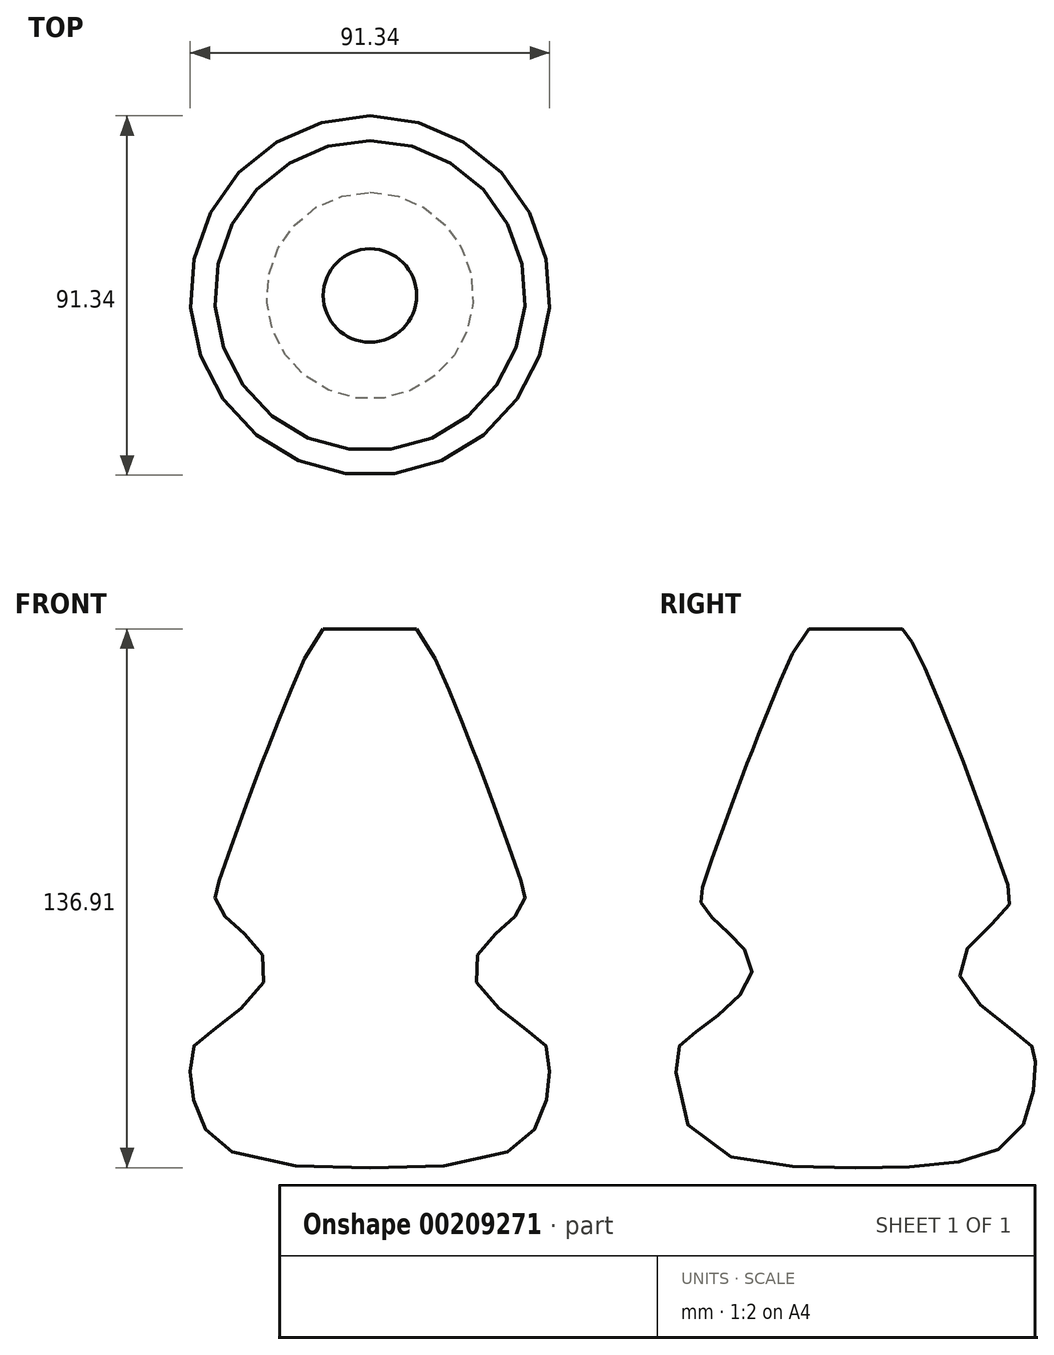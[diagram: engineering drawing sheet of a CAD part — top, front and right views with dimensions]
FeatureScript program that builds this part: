
annotation { "Feature Type Name" : "Feature", "Feature Type Description" : "" }
export const myFeature = defineFeature(function(context is Context, id is Id, definition is map)
    precondition{}
    {
        {
            var Q0;
            Q0=qCreatedBy(makeId("Right.planeOp"),FACE);
            var sketch = newSketch(context, id + "F0", { "sketchPlane" : qUnion([Q0])});
            skFitSpline(sketch, "E0", {"points": [v(11.88, 63.3) * mm, v(15.94, 57.05) * mm, v(26.57, 31.41) * mm, v(28.44, 26.73) * mm, v(38.13, 0) * mm, v(38.13, -8.28) * mm, v(26.26, -23.6) * mm, v(43.45, -41.42) * mm, v(45.64, -46.1) * mm, v(40.64, -65.49) * mm, v(0, -73.61) * mm], "startDerivative": vector(52.85, -63.75) * mm, "endDerivative": vector(-320.72, -0.65) * mm});
            skLineSegment(sketch, "E1", {"start": v(0, 68.92) * mm, "end": v(0, 92.37) * mm});
            skSolve(sketch);
        }
        {
            var Q0;
            Q0=sQuery(id+"F0.wireOp",EDGE,"E0");
            var Q1;
            Q1=sQuery(id+"F0.wireOp",EDGE,"E1");
            revolve(context, id + "F1", {"bodyType" : ToolBodyType.SURFACE, "surfaceEntities" : qUnion([Q0]), "axis" : qUnion([Q1]), "revolveType" : RevolveType.FULL});
        }
    });
